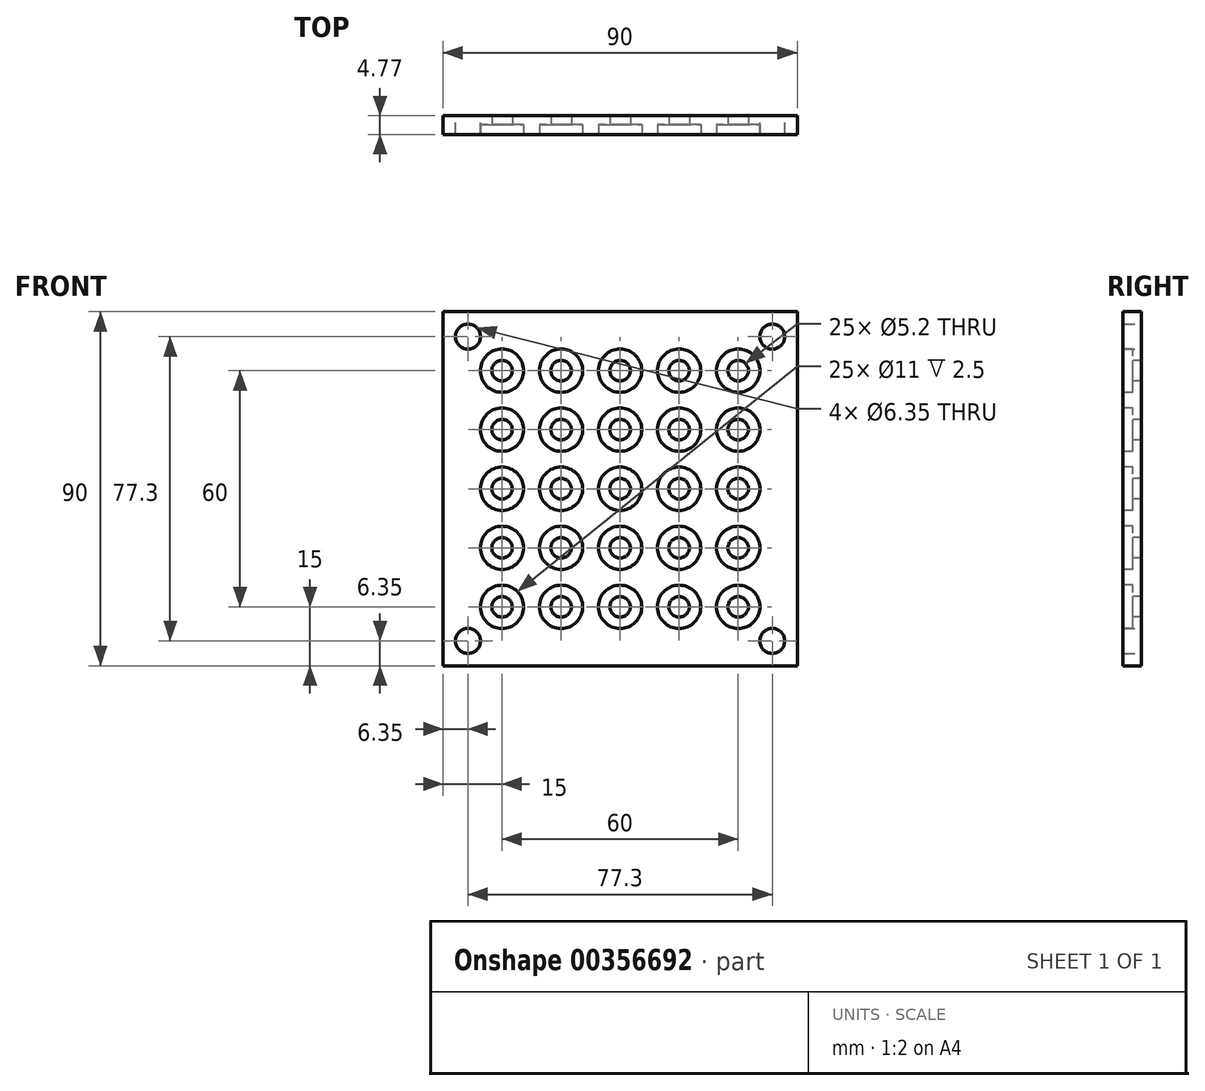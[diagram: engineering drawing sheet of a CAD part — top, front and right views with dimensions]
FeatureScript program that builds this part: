
annotation { "Feature Type Name" : "Feature", "Feature Type Description" : "" }
export const myFeature = defineFeature(function(context is Context, id is Id, definition is map)
    precondition{}
    {
        {
            var Q0;
            Q0=qCreatedBy(makeId("Front.planeOp"),FACE);
            var sketch = newSketch(context, id + "F0", { "sketchPlane" : qUnion([Q0])});
            skLineSegment(sketch, "E0.bottom", {"start": v(-45, 45) * mm, "end": v(45, 45) * mm});
            skLineSegment(sketch, "E0.top", {"start": v(-45, -45) * mm, "end": v(45, -45) * mm});
            skLineSegment(sketch, "E0.left", {"start": v(-45, 45) * mm, "end": v(-45, -45) * mm});
            skLineSegment(sketch, "E0.right", {"start": v(45, 45) * mm, "end": v(45, -45) * mm});
            skCircle(sketch, "E1", {"center": v(-38.65, 38.65) * mm, "radius": 3.18 * mm});
            skCircle(sketch, "E2", {"center": v(38.65, 38.65) * mm, "radius": 3.18 * mm});
            skCircle(sketch, "E3", {"center": v(38.65, -38.65) * mm, "radius": 3.18 * mm});
            skCircle(sketch, "E4", {"center": v(-38.65, -38.65) * mm, "radius": 3.18 * mm});
            skLineSegment(sketch, "E5.bottom", {"start": v(-50, 50) * mm, "end": v(50, 50) * mm, "construction": true});
            skLineSegment(sketch, "E5.top", {"start": v(-50, -50) * mm, "end": v(50, -50) * mm, "construction": true});
            skLineSegment(sketch, "E5.left", {"start": v(-50, 50) * mm, "end": v(-50, -50) * mm, "construction": true});
            skLineSegment(sketch, "E5.right", {"start": v(50, 50) * mm, "end": v(50, -50) * mm, "construction": true});
            skSolve(sketch);
        }
        {
            var Q0;
            Q0=qSketchRegion(id+"F0",true);
            extrude(context, id + "F1", {"entities" : qUnion([Q0]), "depth" : 4.77 * mm});
        }
        {
            var Q0;
            Q0=makeQuery(id+"F1.opExtrude","CAP_FACE",FACE,{"disambiguationData":[OSD([sQuery(id+"F0.wireOp",EDGE,"E0.bottom"),sQuery(id+"F0.wireOp",EDGE,"E0.top"),sQuery(id+"F0.wireOp",EDGE,"E0.left"),sQuery(id+"F0.wireOp",EDGE,"E0.right"),sQuery(id+"F0.wireOp",EDGE,"E1"),sQuery(id+"F0.wireOp",EDGE,"E2"),sQuery(id+"F0.wireOp",EDGE,"E3"),sQuery(id+"F0.wireOp",EDGE,"E4")])],"isStart":false});
            var sketch = newSketch(context, id + "F2", { "sketchPlane" : qUnion([Q0])});
            skCircle(sketch, "E6", {"center": v(-30, 30) * mm, "radius": 2.6 * mm});
            skCircle(sketch, "E7.0.1.0", {"center": v(-30, 15) * mm, "radius": 2.6 * mm});
            skCircle(sketch, "E7.0.2.0", {"center": v(-30, 0) * mm, "radius": 2.6 * mm});
            skCircle(sketch, "E7.0.3.0", {"center": v(-30, -15) * mm, "radius": 2.6 * mm});
            skCircle(sketch, "E7.0.4.0", {"center": v(-30, -30) * mm, "radius": 2.6 * mm});
            skCircle(sketch, "E7.1.0.0", {"center": v(-15, 30) * mm, "radius": 2.6 * mm});
            skCircle(sketch, "E7.1.1.0", {"center": v(-15, 15) * mm, "radius": 2.6 * mm});
            skCircle(sketch, "E7.1.2.0", {"center": v(-15, 0) * mm, "radius": 2.6 * mm});
            skCircle(sketch, "E7.1.3.0", {"center": v(-15, -15) * mm, "radius": 2.6 * mm});
            skCircle(sketch, "E7.1.4.0", {"center": v(-15, -30) * mm, "radius": 2.6 * mm});
            skCircle(sketch, "E7.2.0.0", {"center": v(0, 30) * mm, "radius": 2.6 * mm});
            skCircle(sketch, "E7.2.1.0", {"center": v(0, 15) * mm, "radius": 2.6 * mm});
            skCircle(sketch, "E7.2.2.0", {"center": v(0, 0) * mm, "radius": 2.6 * mm});
            skCircle(sketch, "E7.2.3.0", {"center": v(0, -15) * mm, "radius": 2.6 * mm});
            skCircle(sketch, "E7.2.4.0", {"center": v(0, -30) * mm, "radius": 2.6 * mm});
            skCircle(sketch, "E7.3.0.0", {"center": v(15, 30) * mm, "radius": 2.6 * mm});
            skCircle(sketch, "E7.3.1.0", {"center": v(15, 15) * mm, "radius": 2.6 * mm});
            skCircle(sketch, "E7.3.2.0", {"center": v(15, 0) * mm, "radius": 2.6 * mm});
            skCircle(sketch, "E7.3.3.0", {"center": v(15, -15) * mm, "radius": 2.6 * mm});
            skCircle(sketch, "E7.3.4.0", {"center": v(15, -30) * mm, "radius": 2.6 * mm});
            skCircle(sketch, "E7.4.0.0", {"center": v(30, 30) * mm, "radius": 2.6 * mm});
            skCircle(sketch, "E7.4.1.0", {"center": v(30, 15) * mm, "radius": 2.6 * mm});
            skCircle(sketch, "E7.4.2.0", {"center": v(30, 0) * mm, "radius": 2.6 * mm});
            skCircle(sketch, "E7.4.3.0", {"center": v(30, -15) * mm, "radius": 2.6 * mm});
            skCircle(sketch, "E7.4.4.0", {"center": v(30, -30) * mm, "radius": 2.6 * mm});
            skLineSegment(sketch, "E7.direction1", {"start": v(-30, 30) * mm, "end": v(-15, 30) * mm, "construction": true});
            skLineSegment(sketch, "E7.direction2", {"start": v(-30, 30) * mm, "end": v(-30, 15) * mm, "construction": true});
            skSolve(sketch);
        }
        {
            var Q0;
            Q0=qSketchRegion(id+"F2",true);
            extrude(context, id + "F3", {"entities" : qUnion([Q0]), "operationType" : NewBodyOperationType.REMOVE, "endBound" : BoundingType.UP_TO_NEXT, "oppositeDirection" : true, "depth" : 25 * mm});
        }
        {
            var Q0;
            Q0=makeQuery(id+"F1.opExtrude","CAP_FACE",FACE,{"disambiguationData":[OSD([sQuery(id+"F0.wireOp",EDGE,"E0.bottom"),sQuery(id+"F0.wireOp",EDGE,"E0.top"),sQuery(id+"F0.wireOp",EDGE,"E0.left"),sQuery(id+"F0.wireOp",EDGE,"E0.right"),sQuery(id+"F0.wireOp",EDGE,"E1"),sQuery(id+"F0.wireOp",EDGE,"E2"),sQuery(id+"F0.wireOp",EDGE,"E3"),sQuery(id+"F0.wireOp",EDGE,"E4")])],"isStart":false});
            var sketch = newSketch(context, id + "F4", { "sketchPlane" : qUnion([Q0])});
            skCircle(sketch, "E8", {"center": v(-30, 30) * mm, "radius": 5.5 * mm});
            skCircle(sketch, "E9.0.1.0", {"center": v(-30, 15) * mm, "radius": 5.5 * mm});
            skCircle(sketch, "E9.0.2.0", {"center": v(-30, 0) * mm, "radius": 5.5 * mm});
            skCircle(sketch, "E9.0.3.0", {"center": v(-30, -15) * mm, "radius": 5.5 * mm});
            skCircle(sketch, "E9.0.4.0", {"center": v(-30, -30) * mm, "radius": 5.5 * mm});
            skCircle(sketch, "E9.1.0.0", {"center": v(-15, 30) * mm, "radius": 5.5 * mm});
            skCircle(sketch, "E9.1.1.0", {"center": v(-15, 15) * mm, "radius": 5.5 * mm});
            skCircle(sketch, "E9.1.2.0", {"center": v(-15, 0) * mm, "radius": 5.5 * mm});
            skCircle(sketch, "E9.1.3.0", {"center": v(-15, -15) * mm, "radius": 5.5 * mm});
            skCircle(sketch, "E9.1.4.0", {"center": v(-15, -30) * mm, "radius": 5.5 * mm});
            skCircle(sketch, "E9.2.0.0", {"center": v(0, 30) * mm, "radius": 5.5 * mm});
            skCircle(sketch, "E9.2.1.0", {"center": v(0, 15) * mm, "radius": 5.5 * mm});
            skCircle(sketch, "E9.2.2.0", {"center": v(0, 0) * mm, "radius": 5.5 * mm});
            skCircle(sketch, "E9.2.3.0", {"center": v(0, -15) * mm, "radius": 5.5 * mm});
            skCircle(sketch, "E9.2.4.0", {"center": v(0, -30) * mm, "radius": 5.5 * mm});
            skCircle(sketch, "E9.3.0.0", {"center": v(15, 30) * mm, "radius": 5.5 * mm});
            skCircle(sketch, "E9.3.1.0", {"center": v(15, 15) * mm, "radius": 5.5 * mm});
            skCircle(sketch, "E9.3.2.0", {"center": v(15, 0) * mm, "radius": 5.5 * mm});
            skCircle(sketch, "E9.3.3.0", {"center": v(15, -15) * mm, "radius": 5.5 * mm});
            skCircle(sketch, "E9.3.4.0", {"center": v(15, -30) * mm, "radius": 5.5 * mm});
            skCircle(sketch, "E9.4.0.0", {"center": v(30, 30) * mm, "radius": 5.5 * mm});
            skCircle(sketch, "E9.4.1.0", {"center": v(30, 15) * mm, "radius": 5.5 * mm});
            skCircle(sketch, "E9.4.2.0", {"center": v(30, 0) * mm, "radius": 5.5 * mm});
            skCircle(sketch, "E9.4.3.0", {"center": v(30, -15) * mm, "radius": 5.5 * mm});
            skCircle(sketch, "E9.4.4.0", {"center": v(30, -30) * mm, "radius": 5.5 * mm});
            skLineSegment(sketch, "E9.direction1", {"start": v(-30, 30) * mm, "end": v(-15, 30) * mm, "construction": true});
            skLineSegment(sketch, "E9.direction2", {"start": v(-30, 30) * mm, "end": v(-30, 15) * mm, "construction": true});
            skSolve(sketch);
        }
        {
            var Q0;
            Q0=qSketchRegion(id+"F4",true);
            extrude(context, id + "F5", {"entities" : qUnion([Q0]), "operationType" : NewBodyOperationType.REMOVE, "oppositeDirection" : true, "depth" : 2.5 * mm});
        }
    });
